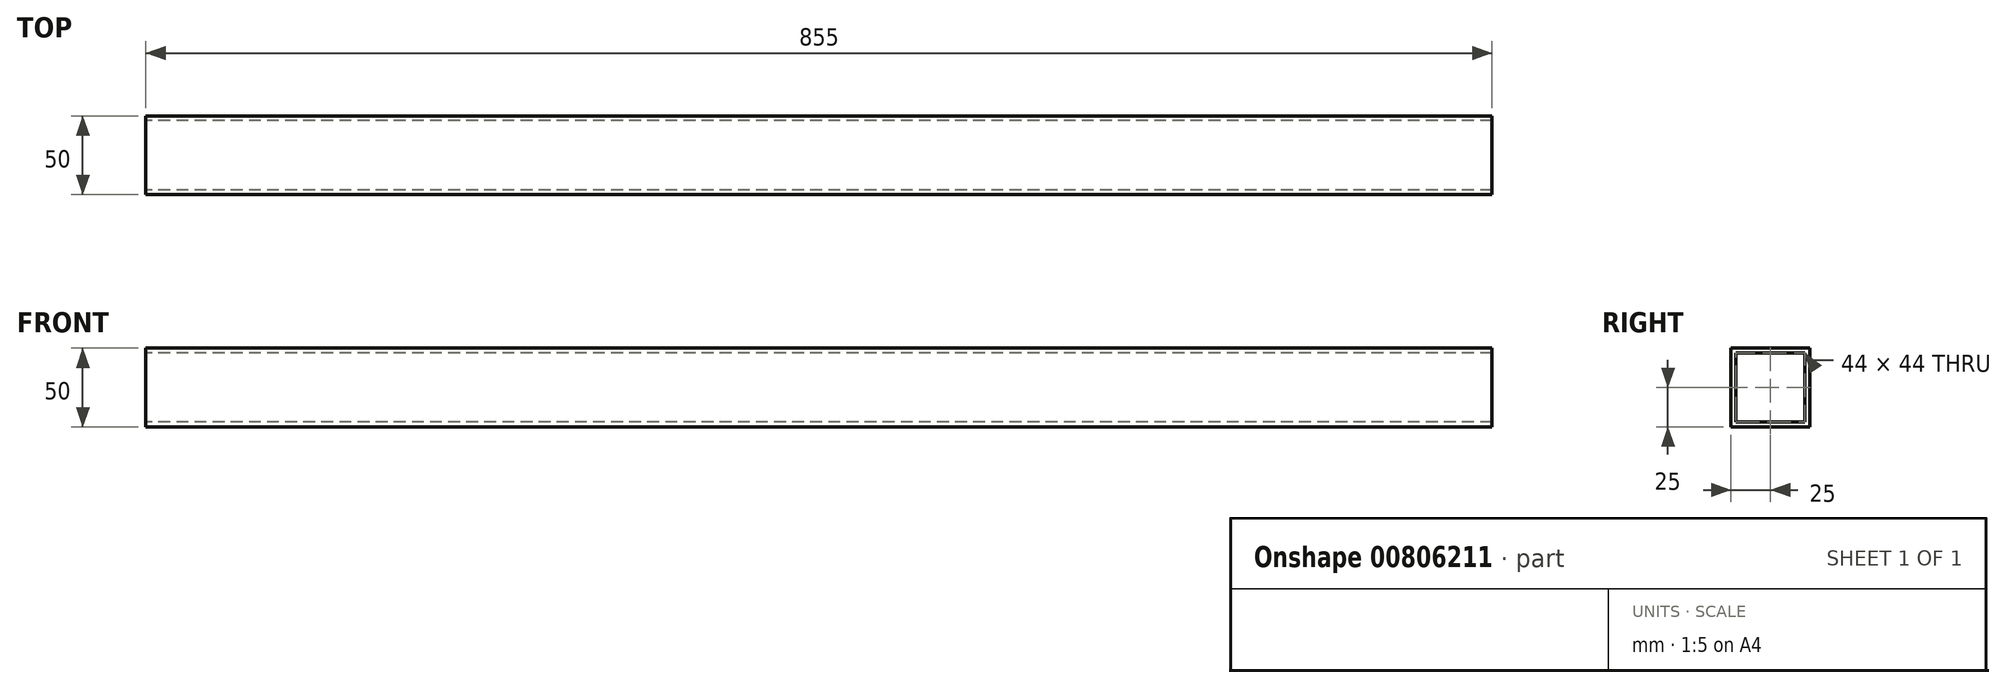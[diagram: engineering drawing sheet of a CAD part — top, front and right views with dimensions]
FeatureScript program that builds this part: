
annotation { "Feature Type Name" : "Feature", "Feature Type Description" : "" }
export const myFeature = defineFeature(function(context is Context, id is Id, definition is map)
    precondition{}
    {
        {
            var Q0;
            Q0=qCreatedBy(makeId("Right.planeOp"),FACE);
            var sketch = newSketch(context, id + "F0", { "sketchPlane" : qUnion([Q0])});
            skLineSegment(sketch, "E0.bottom", {"start": v(25, -25) * mm, "end": v(-25, -25) * mm});
            skLineSegment(sketch, "E0.top", {"start": v(25, 25) * mm, "end": v(-25, 25) * mm});
            skLineSegment(sketch, "E0.left", {"start": v(25, -25) * mm, "end": v(25, 25) * mm});
            skLineSegment(sketch, "E0.right", {"start": v(-25, -25) * mm, "end": v(-25, 25) * mm});
            skPoint(sketch, "E0.middle", {"position": v(0, 0) * mm});
            skLineSegment(sketch, "E1.0", {"start": v(22, 22) * mm, "end": v(-22, 22) * mm});
            skLineSegment(sketch, "E1.1", {"start": v(22, -22) * mm, "end": v(22, 22) * mm});
            skLineSegment(sketch, "E1.2", {"start": v(22, -22) * mm, "end": v(-22, -22) * mm});
            skLineSegment(sketch, "E1.3", {"start": v(-22, -22) * mm, "end": v(-22, 22) * mm});
            skSolve(sketch);
        }
        {
            var Q0;
            Q0=qSketchRegion(id+"F0",true);
            extrude(context, id + "F1", {"entities" : qUnion([Q0]), "depth" : 855 * mm, "offsetDistance" : 25 * mm});
        }
    });
